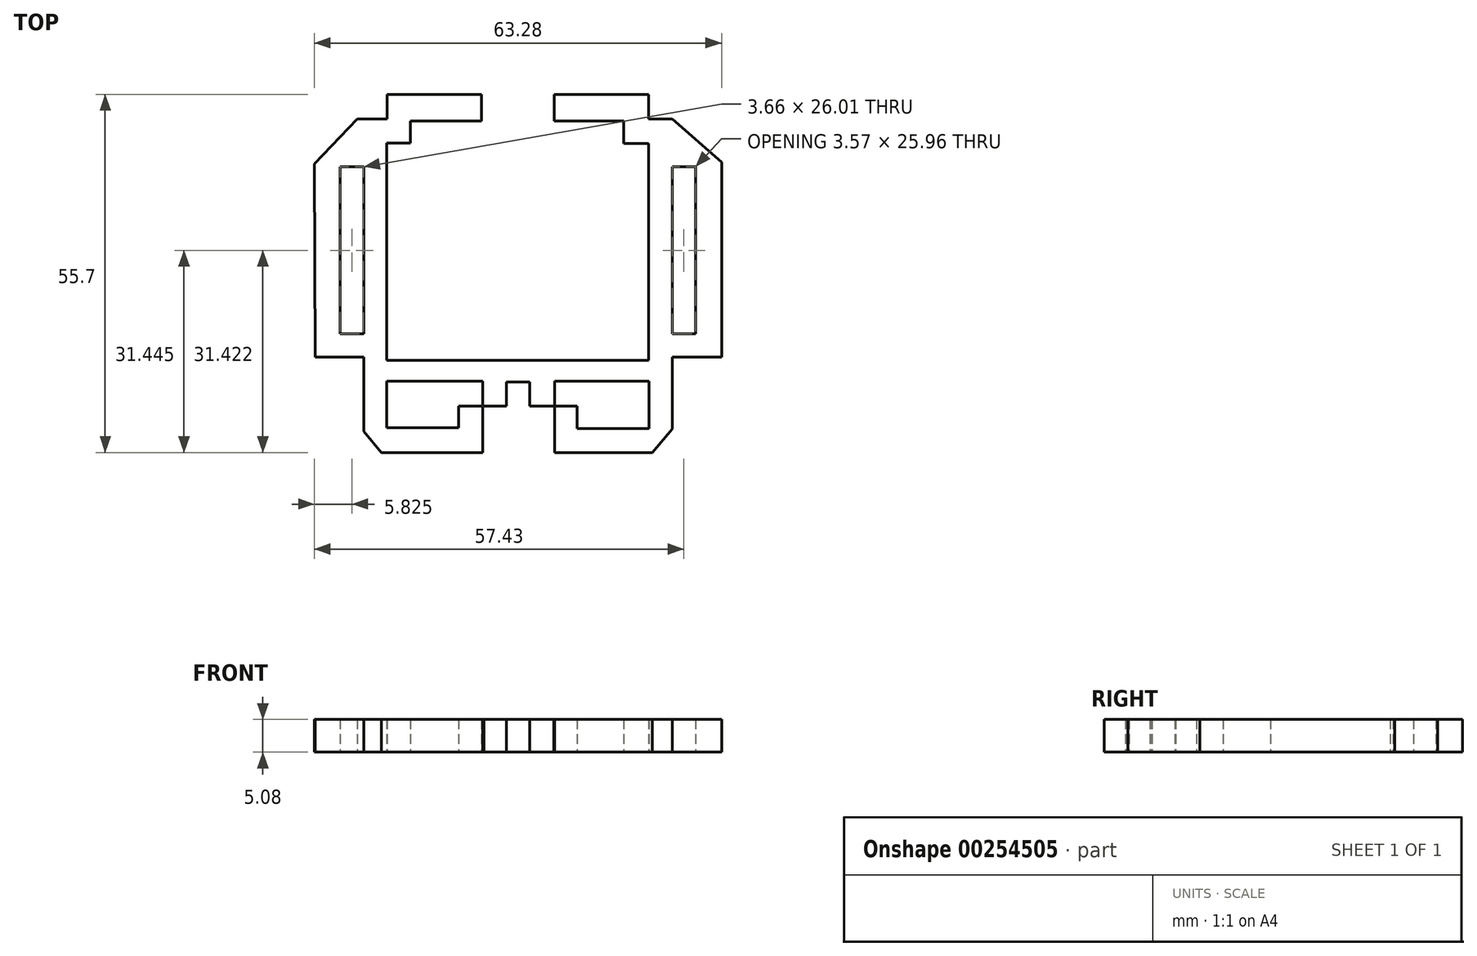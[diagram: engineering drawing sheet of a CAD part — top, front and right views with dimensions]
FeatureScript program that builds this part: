
annotation { "Feature Type Name" : "Feature", "Feature Type Description" : "" }
export const myFeature = defineFeature(function(context is Context, id is Id, definition is map)
    precondition{}
    {
        {
            var Q0;
            Q0=qCreatedBy(makeId("Top.planeOp"),FACE);
            var sketch = newSketch(context, id + "F0", { "sketchPlane" : qUnion([Q0])});
            skLineSegment(sketch, "E0", {"start": v(-33.45, 9.2) * mm, "end": v(-26.8, 16.12) * mm});
            skLineSegment(sketch, "E1", {"start": v(-26.8, 16.12) * mm, "end": v(-22.17, 16.12) * mm});
            skLineSegment(sketch, "E2", {"start": v(-22.17, 16.12) * mm, "end": v(-22.17, 19.99) * mm});
            skLineSegment(sketch, "E3", {"start": v(-22.17, 19.99) * mm, "end": v(-25.8, 19.97) * mm});
            skLineSegment(sketch, "E4", {"start": v(-25.8, 19.97) * mm, "end": v(-25.8, 38.73) * mm});
            skLineSegment(sketch, "E5", {"start": v(-25.8, 38.73) * mm, "end": v(-18.88, 45.9) * mm});
            skLineSegment(sketch, "E6", {"start": v(-18.88, 45.9) * mm, "end": v(14.3, 45.9) * mm});
            skLineSegment(sketch, "E7", {"start": v(14.3, 45.9) * mm, "end": v(22.2, 38.73) * mm});
            skLineSegment(sketch, "E8", {"start": v(22.2, 38.73) * mm, "end": v(22.2, 19.97) * mm});
            skLineSegment(sketch, "E9", {"start": v(22.2, 19.97) * mm, "end": v(18.52, 19.97) * mm});
            skLineSegment(sketch, "E10", {"start": v(18.52, 19.97) * mm, "end": v(18.52, 16.12) * mm});
            skLineSegment(sketch, "E11", {"start": v(18.52, 16.12) * mm, "end": v(22.2, 16.12) * mm});
            skLineSegment(sketch, "E12", {"start": v(22.2, 16.12) * mm, "end": v(29.83, 9.43) * mm});
            skLineSegment(sketch, "E13", {"start": v(29.83, 9.43) * mm, "end": v(29.83, -20.85) * mm});
            skLineSegment(sketch, "E14", {"start": v(29.83, -20.85) * mm, "end": v(22.14, -20.85) * mm});
            skLineSegment(sketch, "E15", {"start": v(22.14, -20.85) * mm, "end": v(22.14, -32.04) * mm});
            skLineSegment(sketch, "E16", {"start": v(22.14, -32.04) * mm, "end": v(19.03, -35.7) * mm});
            skLineSegment(sketch, "E17", {"start": v(19.03, -35.7) * mm, "end": v(3.87, -35.7) * mm});
            skLineSegment(sketch, "E18", {"start": v(3.87, -35.7) * mm, "end": v(3.87, -28.47) * mm});
            skLineSegment(sketch, "E19", {"start": v(3.87, -28.47) * mm, "end": v(-7.29, -28.47) * mm});
            skLineSegment(sketch, "E20", {"start": v(-7.29, -28.47) * mm, "end": v(-7.29, -35.7) * mm});
            skLineSegment(sketch, "E21", {"start": v(-7.29, -35.7) * mm, "end": v(-23.05, -35.7) * mm});
            skLineSegment(sketch, "E22", {"start": v(-23.05, -35.7) * mm, "end": v(-25.8, -32.44) * mm});
            skLineSegment(sketch, "E23", {"start": v(-25.8, -32.44) * mm, "end": v(-25.8, -20.85) * mm});
            skLineSegment(sketch, "E24", {"start": v(-25.8, -20.85) * mm, "end": v(-33.32, -20.85) * mm});
            skLineSegment(sketch, "E25", {"start": v(-33.32, -20.85) * mm, "end": v(-33.45, 9.2) * mm});
            skCircle(sketch, "E26", {"center": v(-11.3, 31.23) * mm, "radius": 5.9 * mm});
            skPoint(sketch, "E26.first.point", {"position": v(-17.19, 30.94) * mm});
            skPoint(sketch, "E26.second.point", {"position": v(-5.4, 31.07) * mm});
            skPoint(sketch, "E26.third.point", {"position": v(-11.26, 25.33) * mm});
            skCircle(sketch, "E27", {"center": v(7.12, 31) * mm, "radius": 5.64 * mm});
            skPoint(sketch, "E27.first.point", {"position": v(1.48, 30.84) * mm});
            skPoint(sketch, "E27.second.point", {"position": v(12.76, 30.78) * mm});
            skPoint(sketch, "E27.third.point", {"position": v(7.1, 36.64) * mm});
            skLineSegment(sketch, "E28.bottom", {"start": v(-14.96, 34.57) * mm, "end": v(-7.5, 34.57) * mm});
            skLineSegment(sketch, "E28.top", {"start": v(-14.96, 27.44) * mm, "end": v(-7.5, 27.44) * mm});
            skLineSegment(sketch, "E28.left", {"start": v(-14.96, 34.57) * mm, "end": v(-14.96, 27.44) * mm});
            skLineSegment(sketch, "E28.right", {"start": v(-7.5, 34.57) * mm, "end": v(-7.5, 27.44) * mm});
            skLineSegment(sketch, "E29.bottom", {"start": v(3.8, 34.28) * mm, "end": v(10.72, 34.28) * mm});
            skLineSegment(sketch, "E29.top", {"start": v(3.8, 27.44) * mm, "end": v(10.72, 27.44) * mm});
            skLineSegment(sketch, "E29.left", {"start": v(3.8, 34.28) * mm, "end": v(3.8, 27.44) * mm});
            skLineSegment(sketch, "E29.right", {"start": v(10.72, 34.28) * mm, "end": v(10.72, 27.44) * mm});
            skLineSegment(sketch, "E30.bottom", {"start": v(7.12, 31) * mm, "end": v(3.8, 31) * mm});
            skLineSegment(sketch, "E30.top", {"start": v(7.12, 34.28) * mm, "end": v(3.8, 34.28) * mm});
            skLineSegment(sketch, "E30.left", {"start": v(7.12, 31) * mm, "end": v(7.12, 34.28) * mm});
            skLineSegment(sketch, "E30.right", {"start": v(3.8, 31) * mm, "end": v(3.8, 34.28) * mm});
            skLineSegment(sketch, "E31.bottom", {"start": v(-11.3, 31.23) * mm, "end": v(-14.96, 31.23) * mm});
            skLineSegment(sketch, "E31.top", {"start": v(-11.3, 34.57) * mm, "end": v(-14.96, 34.57) * mm});
            skLineSegment(sketch, "E31.left", {"start": v(-11.3, 31.23) * mm, "end": v(-11.3, 34.57) * mm});
            skLineSegment(sketch, "E31.right", {"start": v(-14.96, 31.23) * mm, "end": v(-14.96, 34.57) * mm});
            skLineSegment(sketch, "E32.bottom", {"start": v(-3.8, 23.6) * mm, "end": v(0, 23.6) * mm});
            skLineSegment(sketch, "E32.top", {"start": v(-3.8, 19.8) * mm, "end": v(0, 19.8) * mm});
            skLineSegment(sketch, "E32.left", {"start": v(-3.8, 23.6) * mm, "end": v(-3.8, 19.8) * mm});
            skLineSegment(sketch, "E32.right", {"start": v(0, 23.6) * mm, "end": v(0, 19.8) * mm});
            skLineSegment(sketch, "E33.bottom", {"start": v(-7.5, 15.86) * mm, "end": v(3.8, 15.86) * mm});
            skLineSegment(sketch, "E33.top", {"start": v(-7.5, 12.27) * mm, "end": v(3.8, 12.27) * mm});
            skLineSegment(sketch, "E33.left", {"start": v(-7.5, 15.86) * mm, "end": v(-7.5, 12.27) * mm});
            skLineSegment(sketch, "E33.right", {"start": v(3.8, 15.86) * mm, "end": v(3.8, 12.27) * mm});
            skPoint(sketch, "E34.oppositeSnap0", {"position": v(-25.8, -26.64) * mm});
            skLineSegment(sketch, "E34.bottom", {"start": v(-29.45, -9.9) * mm, "end": v(-25.8, -9.9) * mm});
            skLineSegment(sketch, "E34.top", {"start": v(-29.45, -17.27) * mm, "end": v(-25.8, -17.27) * mm});
            skLineSegment(sketch, "E34.left", {"start": v(-29.45, -9.9) * mm, "end": v(-29.45, -17.27) * mm});
            skLineSegment(sketch, "E34.right", {"start": v(-25.8, -9.9) * mm, "end": v(-25.8, -17.27) * mm});
            skLineSegment(sketch, "E35.top", {"start": v(-29.45, 8.74) * mm, "end": v(-25.8, 8.74) * mm});
            skLineSegment(sketch, "E35.left", {"start": v(-29.45, -9.9) * mm, "end": v(-29.45, 8.74) * mm});
            skLineSegment(sketch, "E35.right", {"start": v(-25.8, -9.9) * mm, "end": v(-25.8, 8.74) * mm});
            skLineSegment(sketch, "E36.bottom", {"start": v(22.2, -9.9) * mm, "end": v(25.76, -9.9) * mm});
            skLineSegment(sketch, "E36.top", {"start": v(22.2, -17.27) * mm, "end": v(25.76, -17.27) * mm});
            skLineSegment(sketch, "E36.left", {"start": v(22.2, -9.9) * mm, "end": v(22.2, -17.27) * mm});
            skLineSegment(sketch, "E36.right", {"start": v(25.76, -9.9) * mm, "end": v(25.76, -17.27) * mm});
            skLineSegment(sketch, "E37.top", {"start": v(22.2, 8.7) * mm, "end": v(25.76, 8.7) * mm});
            skLineSegment(sketch, "E37.left", {"start": v(22.2, -9.9) * mm, "end": v(22.2, 8.7) * mm});
            skLineSegment(sketch, "E37.right", {"start": v(25.76, -9.9) * mm, "end": v(25.76, 8.7) * mm});
            skLineSegment(sketch, "E38.bottom", {"start": v(-3.6, -28.47) * mm, "end": v(0, -28.47) * mm});
            skLineSegment(sketch, "E38.top", {"start": v(-3.6, -24.74) * mm, "end": v(0, -24.74) * mm});
            skLineSegment(sketch, "E38.left", {"start": v(-3.6, -28.47) * mm, "end": v(-3.6, -24.74) * mm});
            skLineSegment(sketch, "E38.right", {"start": v(0, -28.47) * mm, "end": v(0, -24.74) * mm});
            skLineSegment(sketch, "E39", {"start": v(-22.24, -24.61) * mm, "end": v(-22.24, -31.85) * mm});
            skLineSegment(sketch, "E40", {"start": v(-22.24, -31.85) * mm, "end": v(-11.06, -31.85) * mm});
            skLineSegment(sketch, "E41", {"start": v(-11.06, -31.85) * mm, "end": v(-11.06, -28.48) * mm});
            skLineSegment(sketch, "E42", {"start": v(-11.06, -28.48) * mm, "end": v(-7.29, -28.47) * mm});
            skLineSegment(sketch, "E43", {"start": v(-7.29, -24.61) * mm, "end": v(-22.24, -24.61) * mm});
            skLineSegment(sketch, "E44", {"start": v(-7.29, -24.61) * mm, "end": v(-7.29, -28.47) * mm});
            skLineSegment(sketch, "E45", {"start": v(3.87, -28.47) * mm, "end": v(3.87, -24.61) * mm});
            skLineSegment(sketch, "E46", {"start": v(3.87, -24.61) * mm, "end": v(18.56, -24.61) * mm});
            skLineSegment(sketch, "E47", {"start": v(18.56, -24.61) * mm, "end": v(18.56, -31.97) * mm});
            skLineSegment(sketch, "E48", {"start": v(18.56, -31.97) * mm, "end": v(7.4, -31.97) * mm});
            skLineSegment(sketch, "E49", {"start": v(7.4, -31.97) * mm, "end": v(7.4, -28.47) * mm});
            skLineSegment(sketch, "E50", {"start": v(7.4, -28.47) * mm, "end": v(3.87, -28.47) * mm});
            skLineSegment(sketch, "E51", {"start": v(-22.17, 19.99) * mm, "end": v(-22.24, 38.23) * mm});
            skLineSegment(sketch, "E52", {"start": v(-22.24, 38.23) * mm, "end": v(-18.48, 38.25) * mm});
            skLineSegment(sketch, "E53", {"start": v(-18.48, 38.25) * mm, "end": v(-18.5, 42.04) * mm});
            skLineSegment(sketch, "E54", {"start": v(-18.5, 42.04) * mm, "end": v(14.76, 42.16) * mm});
            skLineSegment(sketch, "E55", {"start": v(14.76, 42.16) * mm, "end": v(14.78, 38.23) * mm});
            skLineSegment(sketch, "E56", {"start": v(14.78, 38.23) * mm, "end": v(18.52, 38.24) * mm});
            skLineSegment(sketch, "E57", {"start": v(18.52, 38.24) * mm, "end": v(18.52, 19.97) * mm});
            skLineSegment(sketch, "E58", {"start": v(3.8, 15.86) * mm, "end": v(3.8, 19.97) * mm});
            skLineSegment(sketch, "E59", {"start": v(3.8, 19.97) * mm, "end": v(18.52, 19.97) * mm});
            skLineSegment(sketch, "E60", {"start": v(-7.5, 15.86) * mm, "end": v(-7.5, 19.99) * mm});
            skLineSegment(sketch, "E61", {"start": v(-7.5, 19.99) * mm, "end": v(-22.17, 19.99) * mm});
            skLineSegment(sketch, "E62", {"start": v(-22.23, 12.38) * mm, "end": v(-22.23, -21.38) * mm});
            skLineSegment(sketch, "E63", {"start": v(-22.23, -21.38) * mm, "end": v(18.48, -21.38) * mm});
            skLineSegment(sketch, "E64", {"start": v(18.48, -21.38) * mm, "end": v(18.48, 12.34) * mm});
            skLineSegment(sketch, "E65", {"start": v(18.48, 12.34) * mm, "end": v(14.65, 12.34) * mm});
            skLineSegment(sketch, "E66", {"start": v(14.65, 12.34) * mm, "end": v(14.65, 15.86) * mm});
            skLineSegment(sketch, "E67", {"start": v(14.65, 15.86) * mm, "end": v(3.8, 15.86) * mm});
            skLineSegment(sketch, "E68", {"start": v(-22.23, 12.38) * mm, "end": v(-18.53, 12.38) * mm});
            skLineSegment(sketch, "E69", {"start": v(-18.53, 12.38) * mm, "end": v(-18.53, 15.86) * mm});
            skLineSegment(sketch, "E70", {"start": v(-18.53, 15.86) * mm, "end": v(-7.5, 15.86) * mm});
            skLineSegment(sketch, "E71.bottom", {"start": v(-7.42, -28.31) * mm, "end": v(-7.13, -28.31) * mm});
            skLineSegment(sketch, "E71.top", {"start": v(-7.42, -28.63) * mm, "end": v(-7.13, -28.63) * mm});
            skLineSegment(sketch, "E71.left", {"start": v(-7.42, -28.31) * mm, "end": v(-7.42, -28.63) * mm});
            skLineSegment(sketch, "E71.right", {"start": v(-7.13, -28.31) * mm, "end": v(-7.13, -28.63) * mm});
            skLineSegment(sketch, "E72.bottom", {"start": v(3.95, -28.38) * mm, "end": v(3.78, -28.38) * mm});
            skLineSegment(sketch, "E72.top", {"start": v(3.95, -28.56) * mm, "end": v(3.78, -28.56) * mm});
            skLineSegment(sketch, "E72.left", {"start": v(3.95, -28.38) * mm, "end": v(3.95, -28.56) * mm});
            skLineSegment(sketch, "E72.right", {"start": v(3.78, -28.38) * mm, "end": v(3.78, -28.56) * mm});
            skSolve(sketch);
        }
        {
            var Q0;
            Q0=makeQuery(id+"F0.imprint","IMPRINT",FACE,{"disambiguationData":[TD([[makeQuery(id+"F0.imprint","IMPRINT",EDGE,{"derivedFrom":sQuery(id+"F0.wireOp",EDGE,"E0")}),-1.0]])]});
            extrude(context, id + "F1", {"entities" : qUnion([Q0]), "depth" : 5.08 * mm});
        }
    });
